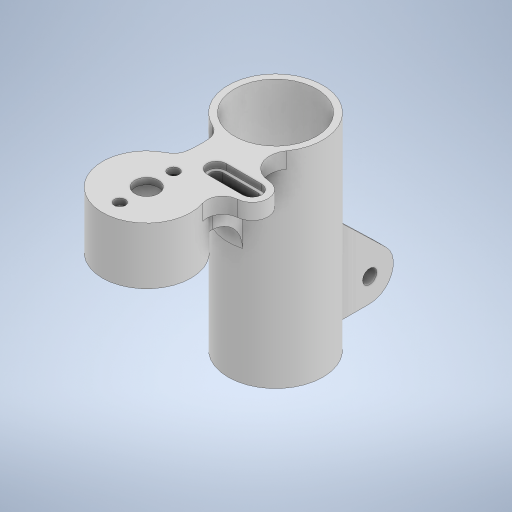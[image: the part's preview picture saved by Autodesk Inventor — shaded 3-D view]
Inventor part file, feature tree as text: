
AUTODESK INVENTOR PART (.ipt)
format: ipt  version: 2024.2 (Build 282272000, 272)  size: 394,752 bytes
history: native  units: mm
features: extrude x7, sketch x7, fillet x3
ambient origin geometry x8: Origin, YZ Plane, XZ Plane, XY Plane, X Axis, Y Axis, Z Axis, Center Point
bodies: Solid1 (feature_tree)
feature tree (17):
  extrude  "Extrusion1"  Depth=28.0mm
  extrude  "Extrusion2"  Depth=35.0mm
  extrude  "Extrusion3"  Depth=18.0mm TaperAngle=0.0deg
  fillet  "Fillet1"  Radius=2.0mm
  fillet  "Fillet2"  Radius=7.5mm
  extrude  "Extrusion4"  Depth=3.5mm
  fillet  "Fillet4"  Radius=8.5mm
  extrude  "Extrusion5"  Depth=26.0mm
  extrude  "Extrusion6"  Depth=18.0mm TaperAngle=0.0deg
  extrude  "Extrusion7"  Depth=5.0mm
  sketch  "Sketch1"  dims[d0=25.5mm d1=28.0mm]
  sketch  "Sketch2"  dims[d2=8.0mm d3=35.0mm]
  sketch  "Sketch3"  dims[d5=15.0mm d6=18.0mm d7=0.0mm d8=2.0mm d9=0.0mm d10=7.5mm]
  sketch  "Sketch5"  dims[d11=3.5mm d12=3.5mm d13=8.5mm]
  sketch  "Sketch6"  dims[d14=8.5mm d15=26.0mm]
  sketch  "Sketch7"  dims[d16=30.0mm d17=47.0mm d18=18.0mm d19=0.0mm d20=0.0mm]
  sketch  "Sketch8"  dims[d21=10.0mm d22=5.0mm d28=4.0mm d29=0.0mm d30=28.0mm d31=13.16045mm d32=5.0mm d33=0.0mm d35=15.0mm d36=4.0mm d37=10.0mm d38=5.0mm d39=7.0mm d40=2.0mm d41=6.0mm d42=2.0mm d43=0.0mm d44=22.0mm d45=4.55mm d46=30.0mm d47=0.0mm d48=15.0mm d49=4.5mm d50=30.0mm d51=0.0mm d52=0.5mm d53=0.872665mm d54=0.5mm d55=0.872665mm]
